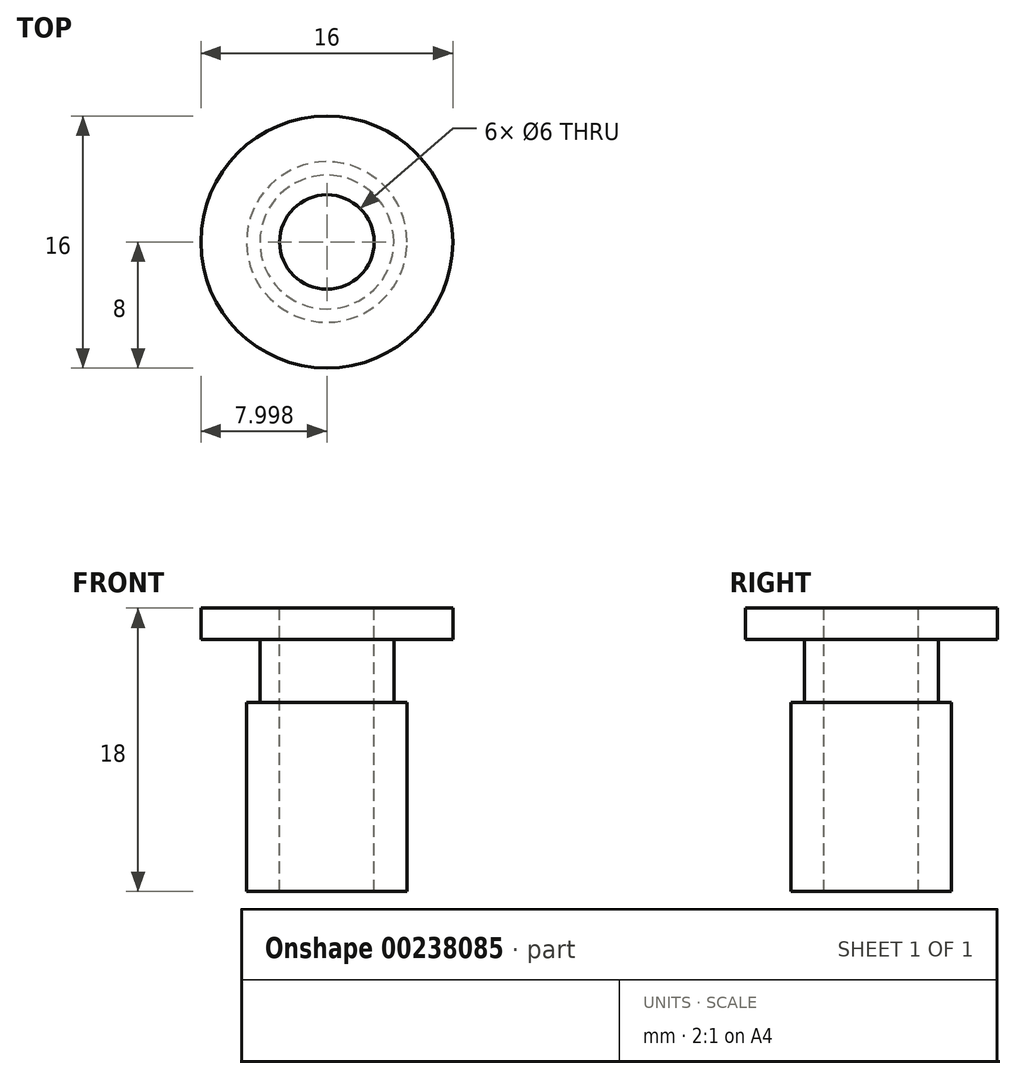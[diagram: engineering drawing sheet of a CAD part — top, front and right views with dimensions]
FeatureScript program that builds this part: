
annotation { "Feature Type Name" : "Feature", "Feature Type Description" : "" }
export const myFeature = defineFeature(function(context is Context, id is Id, definition is map)
    precondition{}
    {
        {
            var Q0;
            Q0=qCreatedBy(makeId("Front.planeOp"),FACE);
            var sketch = newSketch(context, id + "F0", { "sketchPlane" : qUnion([Q0])});
            skLineSegment(sketch, "E0", {"start": v(3.63, 5.93) * mm, "end": v(3.63, -12.07) * mm});
            skLineSegment(sketch, "E1", {"start": v(3.63, -12.07) * mm, "end": v(5.73, -12.07) * mm});
            skLineSegment(sketch, "E2", {"start": v(5.73, -12.07) * mm, "end": v(5.73, -0.07) * mm});
            skLineSegment(sketch, "E3", {"start": v(5.73, -0.07) * mm, "end": v(4.88, -0.07) * mm});
            skLineSegment(sketch, "E4", {"start": v(4.88, -0.07) * mm, "end": v(4.88, 3.93) * mm});
            skLineSegment(sketch, "E5", {"start": v(4.88, 3.93) * mm, "end": v(8.63, 3.93) * mm});
            skLineSegment(sketch, "E6", {"start": v(8.63, 3.93) * mm, "end": v(8.63, 5.93) * mm});
            skLineSegment(sketch, "E7", {"start": v(8.63, 5.93) * mm, "end": v(3.63, 5.93) * mm});
            skLineSegment(sketch, "E8", {"start": v(0.63, 5.92) * mm, "end": v(0.63, -12.66) * mm, "construction": true});
            skSolve(sketch);
        }
        {
            var Q0;
            Q0=makeQuery(id+"F0.imprint","IMPRINT",FACE,{"disambiguationData":[TD([[makeQuery(id+"F0.imprint","IMPRINT",EDGE,{"derivedFrom":sQuery(id+"F0.wireOp",EDGE,"E0")}),1.0]])]});
            var Q1;
            Q1=sQuery(id+"F0.wireOp",EDGE,"E8");
            revolve(context, id + "F1", {"entities" : qUnion([Q0]), "axis" : qUnion([Q1]), "revolveType" : RevolveType.FULL});
        }
    });
